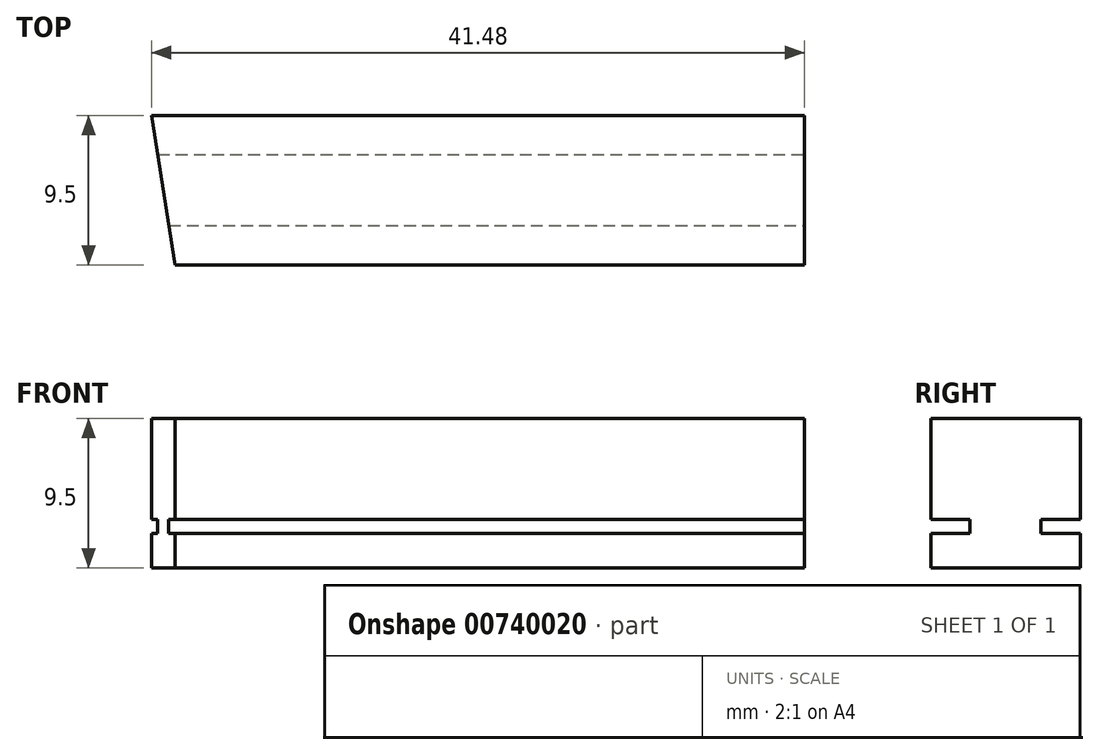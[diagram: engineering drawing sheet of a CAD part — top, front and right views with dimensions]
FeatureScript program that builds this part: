
annotation { "Feature Type Name" : "Feature", "Feature Type Description" : "" }
export const myFeature = defineFeature(function(context is Context, id is Id, definition is map)
    precondition{}
    {
        {
            var Q0;
            Q0=qCreatedBy(makeId("Top.planeOp"),FACE);
            var sketch = newSketch(context, id + "F0", { "sketchPlane" : qUnion([Q0])});
            skLineSegment(sketch, "E0.bottom", {"start": v(-35.47, 24.2) * mm, "end": v(4.53, 24.2) * mm});
            skLineSegment(sketch, "E0.top", {"start": v(-35.47, 14.7) * mm, "end": v(4.53, 14.7) * mm});
            skLineSegment(sketch, "E0.left", {"start": v(-35.47, 24.2) * mm, "end": v(-35.47, 14.7) * mm});
            skLineSegment(sketch, "E0.right", {"start": v(4.53, 24.2) * mm, "end": v(4.53, 14.7) * mm});
            skLineSegment(sketch, "E1", {"start": v(-35.47, 14.7) * mm, "end": v(-36.95, 24.2) * mm});
            skLineSegment(sketch, "E2", {"start": v(-36.95, 24.2) * mm, "end": v(-35.47, 24.2) * mm});
            skSolve(sketch);
        }
        {
            var Q0;
            Q0 = qSketchRegion(id + "F0", true);
            extrude(context, id + "F1", {"entities" : qUnion([Q0]), "depth" : (0.8 + 5 + 2.4 + 0.8 + 0.5) * mm, "offsetDistance" : 25 * mm});
        }
        {
            var Q0;
            Q0=makeQuery(id+"F1.opExtrude","SWEPT_FACE",FACE,{"disambiguationData":[OSD([sQuery(id+"F0.wireOp",EDGE,"E0.right")])]});
            var sketch = newSketch(context, id + "F2", { "sketchPlane" : qUnion([Q0])});
            skLineSegment(sketch, "E3", {"start": v(14.7, 3.1) * mm, "end": v(17.2, 3.1) * mm});
            skLineSegment(sketch, "E4", {"start": v(17.2, 3.1) * mm, "end": v(17.2, 2.2) * mm});
            skLineSegment(sketch, "E5", {"start": v(17.2, 2.2) * mm, "end": v(14.7, 2.2) * mm});
            skLineSegment(sketch, "E6", {"start": v(24.2, 3.1) * mm, "end": v(21.7, 3.1) * mm});
            skLineSegment(sketch, "E7", {"start": v(21.7, 3.1) * mm, "end": v(21.7, 2.2) * mm});
            skLineSegment(sketch, "E8", {"start": v(21.7, 2.2) * mm, "end": v(24.2, 2.2) * mm});
            skSolve(sketch);
        }
        {
            var Q0;
            Q0 = qSketchRegion(id + "F2", true);
            var Q1;
            {var subQ0=sQuery(id+"F2.wireOp",EDGE,"E3");Q1=makeQuery(id+"F2.imprint","IMPRINT",FACE,{"disambiguationData":[TD([[makeQuery(id+"F2.imprint","IMPRINT",EDGE,{"derivedFrom":subQ0}),-1.0]])]});}
            var Q2;
            {var subQ0=sQuery(id+"F2.wireOp",EDGE,"E6");Q2=makeQuery(id+"F2.imprint","IMPRINT",FACE,{"disambiguationData":[TD([[makeQuery(id+"F2.imprint","IMPRINT",EDGE,{"derivedFrom":subQ0}),1.0]])]});}
            extrude(context, id + "F3", {"entities" : qUnion([Q0, Q1, Q2]), "operationType" : NewBodyOperationType.REMOVE, "oppositeDirection" : true, "depth" : 50 * mm, "offsetDistance" : 25 * mm});
        }
    });
